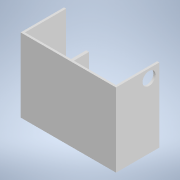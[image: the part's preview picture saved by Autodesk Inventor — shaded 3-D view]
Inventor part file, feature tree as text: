
AUTODESK INVENTOR PART (.ipt)
format: ipt  version: 2020 (Build 240168000, 168)  size: 128,000 bytes
history: native  units: mm
features: extrude x5, sketch x5
ambient origin geometry x8: Origin, YZ Plane, XZ Plane, XY Plane, X Axis, Y Axis, Z Axis, Center Point
bodies: Solid1 (feature_tree)
feature tree (10):
  extrude  "Extrusion1"  Depth=170.0mm
  extrude  "Extrusion2"  Depth=210.0mm
  extrude  "Extrusion3"  Depth=95.0mm TaperAngle=0.0deg
  extrude  "Extrusion4"  Depth=5.0mm
  extrude  "Extrusion5"  Depth=35.0mm TaperAngle=0.0deg
  sketch  "Sketch1"  dims[d0=220.0mm d1=170.0mm]
  sketch  "Sketch2"  dims[d2=100.0mm d3=0.0mm d4=210.0mm]
  sketch  "Sketch3"  dims[d5=240.0mm d6=95.0mm d7=0.0mm]
  sketch  "Sketch4"  dims[d8=5.0mm d9=30.0mm]
  sketch  "Sketch5"  dims[d10=20.0mm d11=45.0mm d12=0.0mm d13=5.0mm d14=10.0mm d15=0.0mm d16=35.0mm d17=0.0mm]
